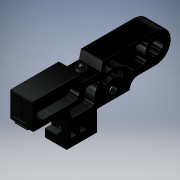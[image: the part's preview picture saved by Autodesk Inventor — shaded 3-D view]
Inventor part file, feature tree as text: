
AUTODESK INVENTOR PART (.ipt)
format: ipt  version: 2017 (Build 210142000, 142)  size: 768,512 bytes
history: native  units: in
note: dims shown in document units (in); Inventor stores cm internally (conversion verified against a paired STEP export)
features: extrude x14, sketch x14, fillet x6, projected_geometry x6, mirror x1
ambient origin geometry x8: Origin, YZ Plane, XZ Plane, XY Plane, X Axis, Y Axis, Z Axis, Center Point
bodies: Solid1 (feature_tree)
feature tree (41):
  extrude  "Extrusion1"  Depth=0.4331in
  extrude  "Extrusion2"  Depth=0.3858in
  extrude  "Extrusion3"  Depth=0.4961in
  fillet  "Fillet1"  Radius=0.8465in
  extrude  "Extrusion4"  Depth=0.5512in
  extrude  "Extrusion5"  Depth=0.0394in
  extrude  "Extrusion6"  Depth=0.315in
  fillet  "Fillet2"  Radius=0.315in
  extrude  "Extrusion7"  Depth=0.1181in
  extrude  "Extrusion8"  Depth=0.1496in
  extrude  "Extrusion9"  Depth=0.0748in
  extrude  "Extrusion10"  Depth=0.2165in
  extrude  "Extrusion11"  Depth=0.0945in TaperAngle=0.0deg
  fillet  "Fillet3"  Radius=0.4331in
  fillet  "Fillet4"  Radius=0.1693in
  fillet  "Fillet5"  Radius=0.3071in
  extrude  "Extrusion12"  Depth=0.1693in TaperAngle=0.0deg
  mirror  "Mirror1"
  fillet  "Fillet6"  Radius=0.0098in
  extrude  "Extrusion13"  Depth=0.4291in
  extrude  "Extrusion14"  Depth=0.1575in
  sketch  "Sketch1"  dims[d0=0.1969in d1=0.4331in]
  sketch  "Sketch2"  dims[d2=1.7717in d3=0.3858in]
  sketch  "Sketch3"  dims[d4=0.4331in d6=0.4961in d8=0.8465in]
  projected_geometry  "Projected Loop1"
  sketch  "Sketch4"  dims[d9=0.5512in d10=0.9055in]
  sketch  "Sketch5"  dims[d12=0.1181in d13=0.0394in]
  sketch  "Sketch6"  dims[d14=0.315in d15=0.0in d16=0.9173in d17=0.315in]
  sketch  "Sketch7"  dims[d18=0.2598in d19=0.1181in]
  projected_geometry  "Projected Loop2"
  sketch  "Sketch8"  dims[d20=0.315in d21=0.0in d22=0.1496in]
  sketch  "Sketch9"  dims[d23=0.0945in d24=0.0in d25=0.0748in]
  projected_geometry  "Projected Loop3"
  sketch  "Sketch10"  dims[d26=0.6102in d27=0.2165in]
  projected_geometry  "Projected Loop4"
  sketch  "Sketch11"  dims[d28=0.1181in d29=0.0945in d30=0.0in d31=0.4331in d32=0.1693in d33=0.0in d34=0.3071in]
  projected_geometry  "Projected Loop5"
  sketch  "Sketch12"  dims[d35=0.2756in d36=0.1693in d37=0.0in d38=0.0098in]
  sketch  "Sketch13"  dims[d39=0.1575in d40=0.4291in]
  sketch  "Sketch14"  dims[d41=0.1693in d42=0.0in d43=0.1575in d44=0.0748in d45=0.0591in d46=0.0748in d47=0.0669in d48=0.1693in d49=0.0in d50=0.0906in d51=0.0906in d52=0.0906in d53=0.0276in d54=0.0276in d55=0.1575in d56=0.1693in d57=0.0in d59=0.1181in d60=0.0787in d61=0.0in d62=0.315in d63=0.0591in d64=0.0984in d65=0.0591in d66=0.0591in d67=0.315in d68=0.0984in d69=0.0787in d71=0.0787in d72=0.0591in d73=0.0591in d74=0.0787in d75=0.0787in d76=0.0787in d77=0.0787in d78=0.128in d79=0.0in d80=0.0787in d81=0.0394in d82=0.0197in d83=0.0039in d84=0.0in d85=0.0079in d86=0.0295in d87=0.0758in d88=0.0295in d89=0.0295in d90=0.0758in d91=1.5748in d93=0.061in d94=0.3937in d96=0.3937in d98=0.1772in d99=0.0in d100=0.0335in d101=0.0906in d102=0.0472in d103=0.1378in d104=0.2835in d105=0.0148in d106=0.0in]
  projected_geometry  "Projected Loop6"
